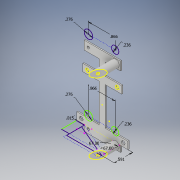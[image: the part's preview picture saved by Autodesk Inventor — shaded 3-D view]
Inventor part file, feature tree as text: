
AUTODESK INVENTOR PART (.ipt)
format: ipt  version: 2018 (Build 220112000, 112)  size: 279,040 bytes
history: native  units: in
note: dims shown in document units (in); Inventor stores cm internally (conversion verified against a paired STEP export)
features: extrude x10, sketch x8
ambient origin geometry x8: Origin, YZ Plane, XZ Plane, XY Plane, X Axis, Y Axis, Z Axis, Center Point
bodies: Solid1 (feature_tree)
feature tree (18):
  extrude  "Extrusion1"  Depth=1.2598in
  extrude  "Extrusion2"  TaperAngle=0.0deg  [1 undecoded]
  extrude  "Extrusion3"  Depth=0.2362in
  extrude  "Extrusion5"  Depth=0.0394in TaperAngle=0.0deg
  extrude  "Extrusion6"  Depth=0.6791in
  extrude  "Extrusion9"  Depth=0.1181in
  extrude  "Extrusion14"  Depth=0.9646in
  extrude  "Extrusion19"  Depth=0.0394in
  extrude  "Extrusion20"  Depth=0.0394in
  extrude  "Extrusion21"  Depth=0.0394in
  sketch  "Sketch18"  dims[d18=0.4823in d19=0.4823in d20=0.1181in d21=0.1181in d22=0.0787in d23=0.0in d28=2.2835in d30=0.0in d31=0.0in d32=0.1969in d33=1.1811in d34=1.1811in d35=0.2756in d36=0.2756in d37=0.0787in d38=0.0787in d39=0.0787in d40=0.0787in d41=0.9055in d42=0.9055in d43=0.4528in d44=0.4528in d45=0.4528in d46=0.4528in d47=0.0394in d48=0.0in d52=0.2756in d55=0.2756in d57=0.0787in d58=0.0in d59=0.2362in d60=0.2362in d61=0.2362in d62=0.2362in d63=0.0787in d64=0.0in d65=1.4567in d66=1.4567in d72=0.4604in d73=0.25in d74=0.0in d97=0.2362in d98=0.8661in d99=0.2362in d100=0.8661in d101=0.4724in d102=0.0in d116=1.378in d117=0.2362in d118=0.2362in d119=0.2362in d120=0.2362in d121=0.8661in d122=0.8661in d123=0.4331in d124=0.4331in d125=0.4331in d126=0.4331in d139=0.0154in d140=0.5906in d141=0.4604in d152=0.75in d153=0.0in d155=0.5in d156=5.0in d157=0.0in d158=0.1969in d159=0.0in d160=0.0787in d162=0.0787in d163=0.3869in]
  sketch  "Sketch1"  dims[d0=0.1969in d2=1.2598in]
  sketch  "Sketch2"  dims[d3=0.2362in d4=0.0in]
  sketch  "Sketch4"  dims[d5=1.6535in d6=0.2362in]
  sketch  "Sketch6"  dims[d7=0.0in d8=0.0394in d9=0.0in]
  sketch  "Sketch13"  dims[d10=1.3583in d13=0.6791in]
  sketch  "Sketch16"  dims[d14=0.6791in d15=0.1181in]
  sketch  "Sketch17"  dims[d16=0.1181in d17=0.9646in]
note: 1 required parameter value undecoded (feature->parameter linkage not recoverable at this tier; creation-order binding heuristic only, values carry confidence <= 0.55)
